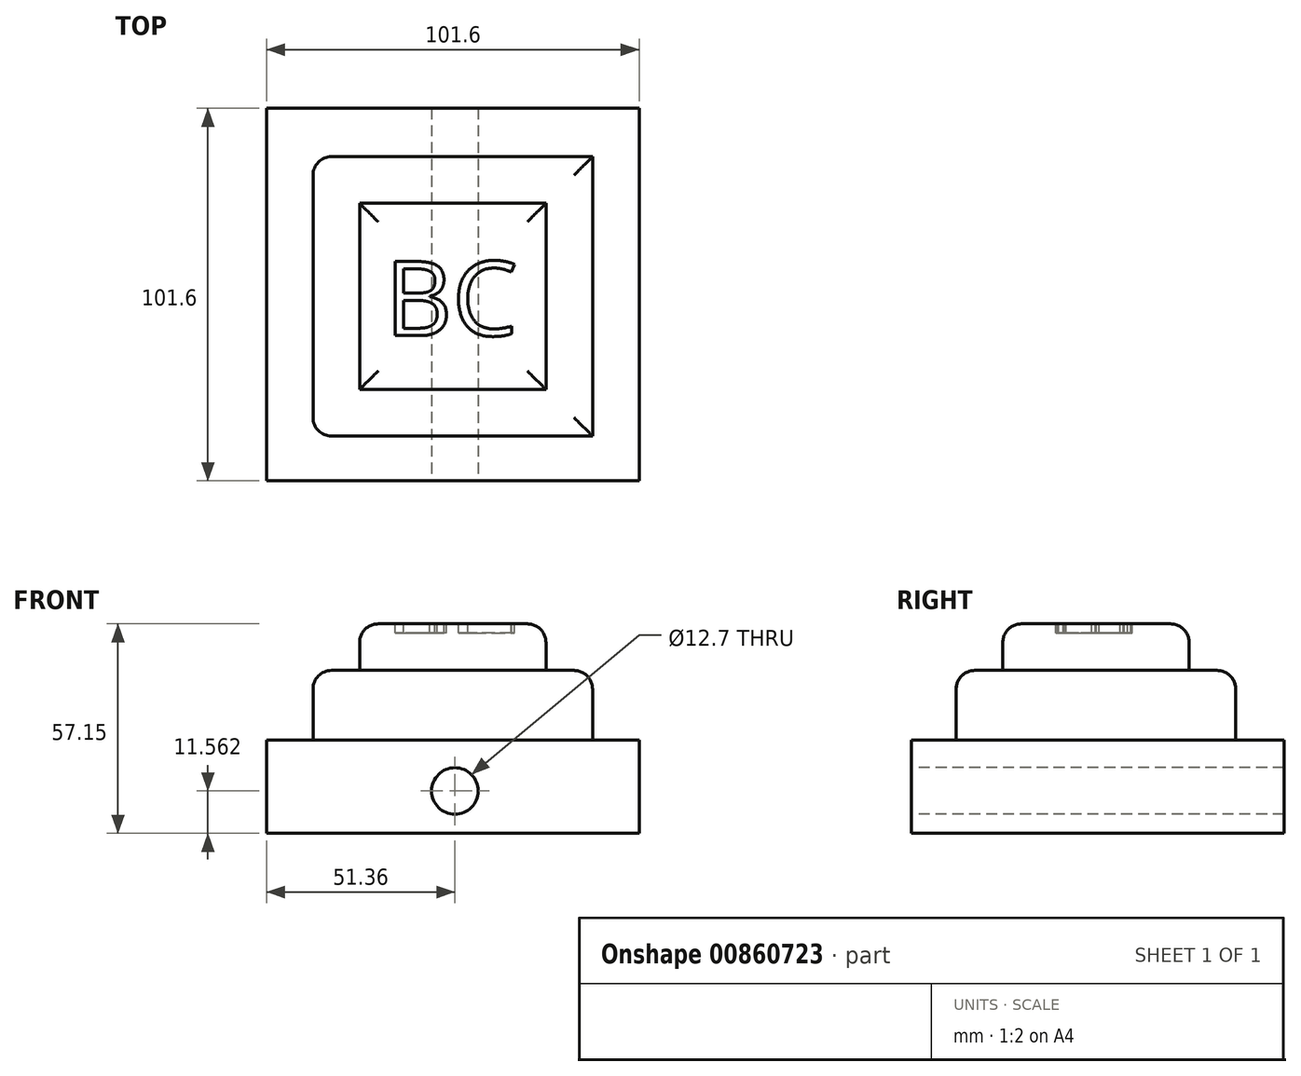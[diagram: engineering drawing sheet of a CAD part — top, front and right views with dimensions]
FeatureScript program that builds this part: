
annotation { "Feature Type Name" : "Feature", "Feature Type Description" : "" }
export const myFeature = defineFeature(function(context is Context, id is Id, definition is map)
    precondition{}
    {
        {
            var Q0;
            Q0=qCreatedBy(makeId("Top.planeOp"),FACE);
            var sketch = newSketch(context, id + "F0", { "sketchPlane" : qUnion([Q0])});
            skLineSegment(sketch, "E0", {"start": v(0, 0) * mm, "end": v(0, 101.6) * mm});
            skLineSegment(sketch, "E1", {"start": v(0, 101.6) * mm, "end": v(101.6, 101.6) * mm});
            skLineSegment(sketch, "E2", {"start": v(101.6, 101.6) * mm, "end": v(101.6, 0) * mm});
            skLineSegment(sketch, "E3", {"start": v(101.6, 0) * mm, "end": v(0, 0) * mm});
            skSolve(sketch);
        }
        {
            var Q0;
            Q0=makeQuery(id+"F0.imprint","IMPRINT",FACE,{"disambiguationData":[TD([[makeQuery(id+"F0.imprint","IMPRINT",EDGE,{"derivedFrom":sQuery(id+"F0.wireOp",EDGE,"E0")}),-1.0]])]});
            extrude(context, id + "F1", {"entities" : qUnion([Q0]), "depth" : 25.4 * mm, "offsetDistance" : 25.4 * mm});
        }
        {
            var Q0;
            Q0=makeQuery(id+"F1.opExtrude","CAP_FACE",FACE,{"disambiguationData":[OSD([sQuery(id+"F0.wireOp",EDGE,"E0"),sQuery(id+"F0.wireOp",EDGE,"E1"),sQuery(id+"F0.wireOp",EDGE,"E2"),sQuery(id+"F0.wireOp",EDGE,"E3")])],"isStart":false});
            var sketch = newSketch(context, id + "F2", { "sketchPlane" : qUnion([Q0])});
            skLineSegment(sketch, "E4", {"start": v(12.67, 88.41) * mm, "end": v(12.67, 12.21) * mm});
            skLineSegment(sketch, "E5", {"start": v(12.67, 12.21) * mm, "end": v(88.87, 12.21) * mm});
            skLineSegment(sketch, "E6", {"start": v(88.87, 12.21) * mm, "end": v(88.87, 88.41) * mm});
            skLineSegment(sketch, "E7", {"start": v(12.67, 88.41) * mm, "end": v(88.87, 88.41) * mm});
            skSolve(sketch);
        }
        {
            var Q0;
            Q0=makeQuery(id+"F2.imprint","IMPRINT",FACE,{"disambiguationData":[TD([[makeQuery(id+"F2.imprint","IMPRINT",EDGE,{"derivedFrom":sQuery(id+"F2.wireOp",EDGE,"E4")}),1.0]])]});
            extrude(context, id + "F3", {"entities" : qUnion([Q0]), "depth" : 19.05 * mm, "offsetDistance" : 25.4 * mm});
        }
        {
            var Q0;
            Q0=makeQuery(id+"F3.opExtrude","CAP_FACE",FACE,{"disambiguationData":[OSD([sQuery(id+"F2.wireOp",EDGE,"E4"),sQuery(id+"F2.wireOp",EDGE,"E5"),sQuery(id+"F2.wireOp",EDGE,"E6"),sQuery(id+"F2.wireOp",EDGE,"E7")])],"isStart":false});
            var sketch = newSketch(context, id + "F4", { "sketchPlane" : qUnion([Q0])});
            skLineSegment(sketch, "E8", {"start": v(25.37, 75.71) * mm, "end": v(25.37, 24.91) * mm});
            skLineSegment(sketch, "E9", {"start": v(25.37, 24.91) * mm, "end": v(76.17, 24.91) * mm});
            skLineSegment(sketch, "E10", {"start": v(76.17, 24.91) * mm, "end": v(76.17, 75.71) * mm});
            skLineSegment(sketch, "E11", {"start": v(76.17, 75.71) * mm, "end": v(25.37, 75.71) * mm});
            skSolve(sketch);
        }
        {
            var Q0;
            Q0=makeQuery(id+"F4.imprint","IMPRINT",FACE,{"disambiguationData":[TD([[makeQuery(id+"F4.imprint","IMPRINT",EDGE,{"derivedFrom":sQuery(id+"F4.wireOp",EDGE,"E8")}),1.0]])]});
            extrude(context, id + "F5", {"entities" : qUnion([Q0]), "depth" : 12.7 * mm, "offsetDistance" : 25.4 * mm});
        }
        {
            var Q0;
            Q0=makeQuery(id+"F1.opExtrude","SWEPT_FACE",FACE,{"disambiguationData":[OSD([sQuery(id+"F0.wireOp",EDGE,"E3")])]});
            var sketch = newSketch(context, id + "F6", { "sketchPlane" : qUnion([Q0])});
            skCircle(sketch, "E12", {"center": v(51.36, 11.56) * mm, "radius": 6.35 * mm});
            skSolve(sketch);
        }
        {
            var Q0;
            Q0=makeQuery(id+"F6.imprint","IMPRINT",FACE,{"disambiguationData":[TD([[makeQuery(id+"F6.imprint","IMPRINT",EDGE,{"derivedFrom":sQuery(id+"F6.wireOp",EDGE,"E12")}),1.0]])]});
            extrude(context, id + "F7", {"entities" : qUnion([Q0]), "operationType" : NewBodyOperationType.REMOVE, "oppositeDirection" : true, "depth" : 101.6 * mm, "offsetDistance" : 25.4 * mm});
        }
        {
            var Q0;
            Q0=makeQuery(id+"F3.opExtrude","CAP_EDGE",EDGE,{"disambiguationData":[OSD([sQuery(id+"F2.wireOp",EDGE,"E4")])],"isStart":false});
            fillet(context, id + "F8", {"entities" : qUnion([Q0]), "radius" : 5.08 * mm, "tangentPropagation" : true, "allowEdgeOverflow" : false});
        }
        {
            var Q0;
            Q0=makeQuery(id+"F3.opExtrude","CAP_EDGE",EDGE,{"disambiguationData":[OSD([sQuery(id+"F2.wireOp",EDGE,"E6")])],"isStart":false});
            var Q1;
            Q1=makeQuery(id+"F3.opExtrude","CAP_FACE",FACE,{"disambiguationData":[OSD([sQuery(id+"F2.wireOp",EDGE,"E4"),sQuery(id+"F2.wireOp",EDGE,"E5"),sQuery(id+"F2.wireOp",EDGE,"E6"),sQuery(id+"F2.wireOp",EDGE,"E7")])],"isStart":false});
            fillet(context, id + "F9", {"entities" : qUnion([Q0, Q1]), "radius" : 5.08 * mm, "tangentPropagation" : true, "allowEdgeOverflow" : false});
        }
        {
            var Q0;
            Q0=makeQuery(id+"F5.opExtrude","CAP_FACE",FACE,{"disambiguationData":[OSD([sQuery(id+"F4.wireOp",EDGE,"E8"),sQuery(id+"F4.wireOp",EDGE,"E9"),sQuery(id+"F4.wireOp",EDGE,"E10"),sQuery(id+"F4.wireOp",EDGE,"E11")])],"isStart":false});
            fillet(context, id + "F10", {"entities" : qUnion([Q0]), "radius" : 5.08 * mm, "tangentPropagation" : true, "allowEdgeOverflow" : false});
        }
        {
            var Q0;
            Q0=makeQuery(id+"F5.opExtrude","CAP_FACE",FACE,{"disambiguationData":[OSD([sQuery(id+"F4.wireOp",EDGE,"E8"),sQuery(id+"F4.wireOp",EDGE,"E9"),sQuery(id+"F4.wireOp",EDGE,"E10"),sQuery(id+"F4.wireOp",EDGE,"E11")])],"isStart":false});
            var sketch = newSketch(context, id + "F11", { "sketchPlane" : qUnion([Q0])});
            skText(sketch, "E13", { "text": "BC", "fontName": "OpenSans-Regular.ttf"});
            const initialGuessF11  = {"E13": [0.03226, 0.03963, 1, 0, 0.0204]};
            skSetInitialGuess(sketch, initialGuessF11);
            skSolve(sketch);
        }
        {
            var Q0;
            Q0 = qSketchRegion(id + "F11", true);
            extrude(context, id + "F12", {"entities" : qUnion([Q0]), "operationType" : NewBodyOperationType.REMOVE, "oppositeDirection" : true, "depth" : 2.54 * mm, "offsetDistance" : 25.4 * mm});
        }
    });
